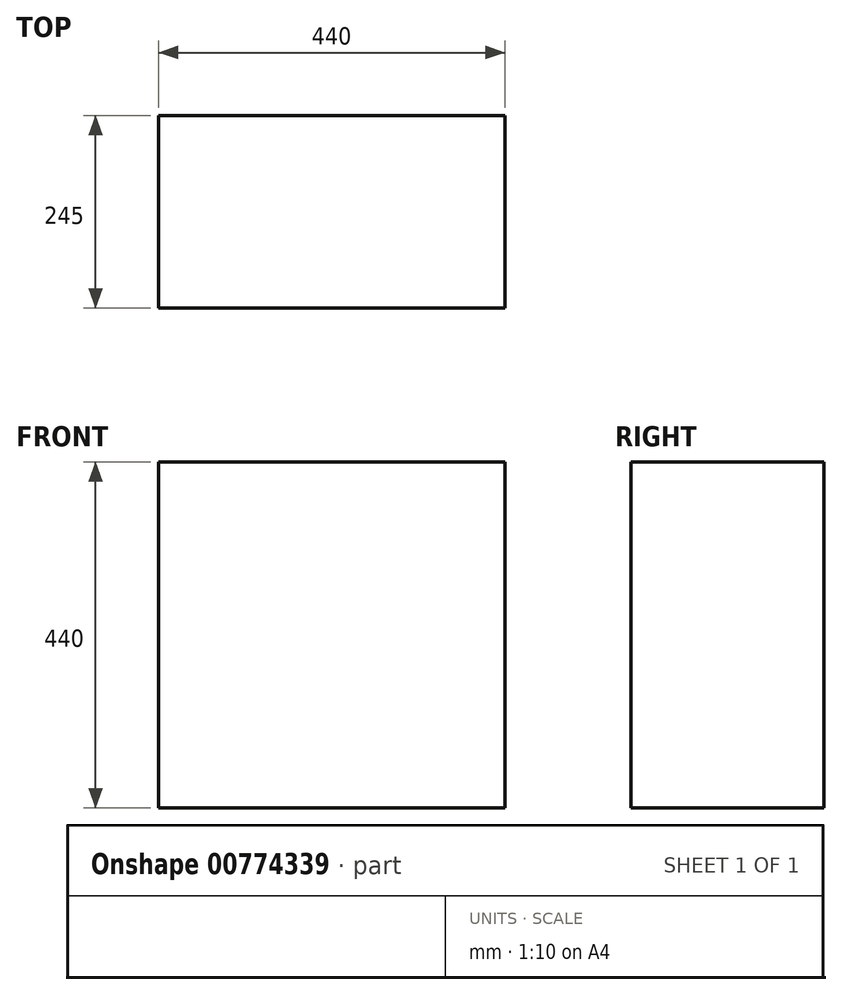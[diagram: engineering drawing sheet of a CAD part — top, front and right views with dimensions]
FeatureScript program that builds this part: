
annotation { "Feature Type Name" : "Feature", "Feature Type Description" : "" }
export const myFeature = defineFeature(function(context is Context, id is Id, definition is map)
    precondition{}
    {
        {
            var Q0;
            Q0=qCreatedBy(makeId("Front.planeOp"),FACE);
            var sketch = newSketch(context, id + "F0", { "sketchPlane" : qUnion([Q0])});
            skLineSegment(sketch, "E0.bottom", {"start": v(0, 0) * mm, "end": v(440, 0) * mm});
            skLineSegment(sketch, "E0.top", {"start": v(0, 440) * mm, "end": v(440, 440) * mm});
            skLineSegment(sketch, "E0.left", {"start": v(0, 0) * mm, "end": v(0, 440) * mm});
            skLineSegment(sketch, "E0.right", {"start": v(440, 0) * mm, "end": v(440, 440) * mm});
            skSolve(sketch);
        }
        {
            var Q0;
            Q0=makeQuery(id+"F0.imprint","IMPRINT",FACE,{"disambiguationData":[TD([[makeQuery(id+"F0.imprint","IMPRINT",EDGE,{"derivedFrom":sQuery(id+"F0.wireOp",EDGE,"E0.bottom")}),1.0]])]});
            extrude(context, id + "F1", {"entities" : qUnion([Q0]), "depth" : 245 * mm, "offsetDistance" : 25 * mm});
        }
    });
